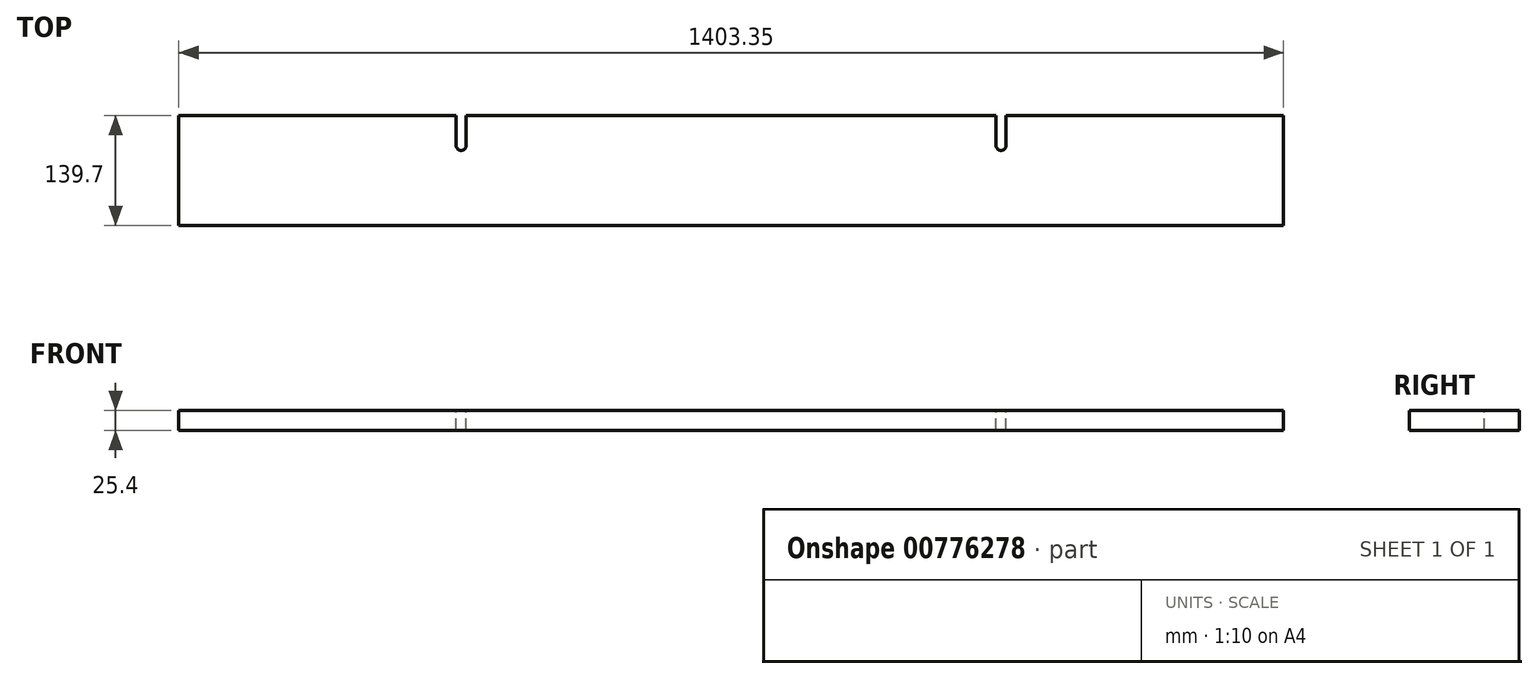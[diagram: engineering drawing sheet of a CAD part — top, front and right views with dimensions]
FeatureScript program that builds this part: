
annotation { "Feature Type Name" : "Feature", "Feature Type Description" : "" }
export const myFeature = defineFeature(function(context is Context, id is Id, definition is map)
    precondition{}
    {
        {
            var Q0;
            Q0=qCreatedBy(makeId("Top.planeOp"),FACE);
            var sketch = newSketch(context, id + "F0", { "sketchPlane" : qUnion([Q0])});
            skLineSegment(sketch, "E0.bottom", {"start": v(-439.02, 91.42) * mm, "end": v(964.33, 91.42) * mm});
            skLineSegment(sketch, "E0.top", {"start": v(-439.02, -48.28) * mm, "end": v(964.33, -48.28) * mm});
            skLineSegment(sketch, "E0.left", {"start": v(-439.02, 91.42) * mm, "end": v(-439.02, -48.28) * mm});
            skLineSegment(sketch, "E0.right", {"start": v(964.33, 91.42) * mm, "end": v(964.33, -48.28) * mm});
            skSolve(sketch);
        }
        {
            var Q0;
            Q0 = qSketchRegion(id + "F0", true);
            extrude(context, id + "F1", {"entities" : qUnion([Q0]), "depth" : 25.4 * mm, "offsetDistance" : 25.4 * mm});
        }
        {
            var Q0;
            Q0=makeQuery(id+"F1.opExtrude","CAP_FACE",FACE,{"disambiguationData":[OSD([sQuery(id+"F0.wireOp",EDGE,"E0.bottom"),sQuery(id+"F0.wireOp",EDGE,"E0.top"),sQuery(id+"F0.wireOp",EDGE,"E0.left"),sQuery(id+"F0.wireOp",EDGE,"E0.right")])],"isStart":false});
            var sketch = newSketch(context, id + "F2", { "sketchPlane" : qUnion([Q0])});
            skArc(sketch, "E1", {"start": v(599.2, 53.32) * mm, "mid": v(605.55, 46.97) * mm, "end": v(611.9, 53.32) * mm});
            skArc(sketch, "E2", {"start": v(-86.6, 53.32) * mm, "mid": v(-80.25, 46.97) * mm, "end": v(-73.9, 53.32) * mm});
            skLineSegment(sketch, "E3", {"start": v(-86.6, 114.5) * mm, "end": v(-86.6, 53.32) * mm});
            skLineSegment(sketch, "E4", {"start": v(-73.9, 119.78) * mm, "end": v(-73.9, 53.32) * mm});
            skLineSegment(sketch, "E5", {"start": v(-73.9, 119.78) * mm, "end": v(-86.6, 114.5) * mm});
            skLineSegment(sketch, "E6", {"start": v(599.2, 106.17) * mm, "end": v(599.2, 53.32) * mm});
            skLineSegment(sketch, "E7", {"start": v(611.9, 112.72) * mm, "end": v(611.9, 53.32) * mm});
            skLineSegment(sketch, "E8", {"start": v(611.9, 112.72) * mm, "end": v(599.2, 106.17) * mm});
            skSolve(sketch);
        }
        {
            var Q0;
            Q0 = qSketchRegion(id + "F2", true);
            extrude(context, id + "F3", {"entities" : qUnion([Q0]), "operationType" : NewBodyOperationType.REMOVE, "endBound" : BoundingType.THROUGH_ALL, "oppositeDirection" : true, "depth" : 25.4 * mm, "offsetDistance" : 25.4 * mm});
        }
    });
